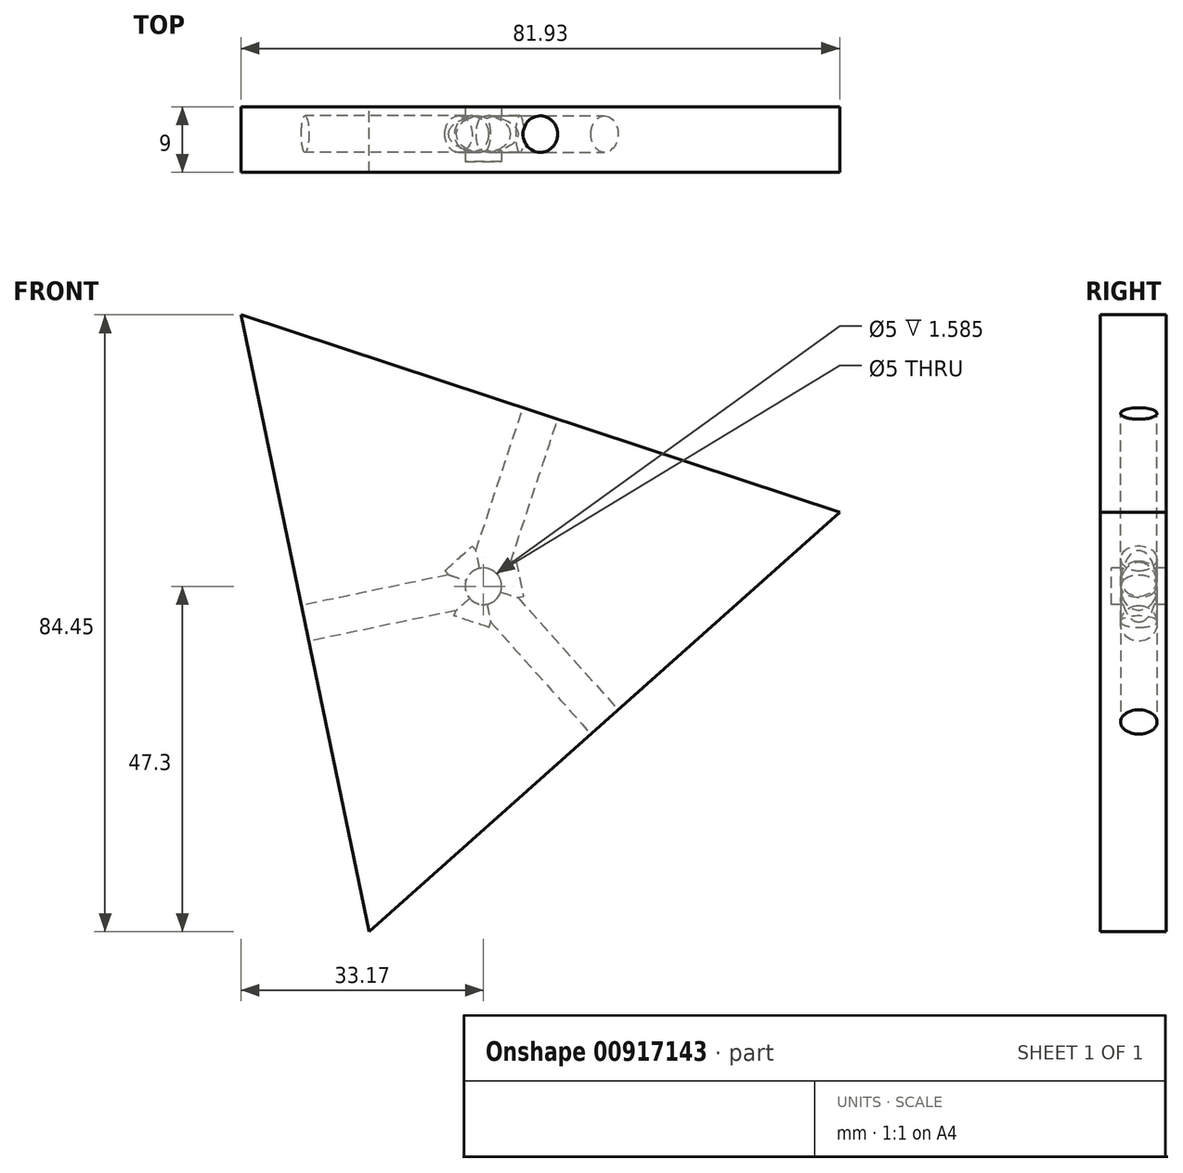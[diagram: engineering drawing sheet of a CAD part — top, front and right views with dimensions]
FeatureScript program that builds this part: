
annotation { "Feature Type Name" : "Feature", "Feature Type Description" : "" }
export const myFeature = defineFeature(function(context is Context, id is Id, definition is map)
    precondition{}
    {
        {
            var Q0;
            Q0=qCreatedBy(makeId("Front.planeOp"),FACE);
            var sketch = newSketch(context, id + "F0", { "sketchPlane" : qUnion([Q0])});
            skCircle(sketch, "E0.cCircle", {"center": v(0, 0) * mm, "radius": 24.9 * mm, "construction": true});
            skLineSegment(sketch, "E0.0", {"start": v(-33.17, 37.15) * mm, "end": v(48.76, 10.15) * mm});
            skLineSegment(sketch, "E0.1", {"start": v(48.76, 10.15) * mm, "end": v(-15.6, -47.3) * mm});
            skLineSegment(sketch, "E0.2", {"start": v(-15.6, -47.3) * mm, "end": v(-33.17, 37.15) * mm});
            skPoint(sketch, "E0.0.midPoint", {"position": v(7.8, 23.65) * mm});
            skSolve(sketch);
        }
        {
            var Q0;
            Q0 = qSketchRegion(id + "F0", true);
            extrude(context, id + "F1", {"entities" : qUnion([Q0]), "depth" : 7.5 * mm, "offsetDistance" : 25 * mm});
        }
        {
            var Q0;
            Q0=makeQuery(id+"F1.opExtrude","CAP_FACE",FACE,{"disambiguationData":[OSD([sQuery(id+"F0.wireOp",EDGE,"E0.0"),sQuery(id+"F0.wireOp",EDGE,"E0.1"),sQuery(id+"F0.wireOp",EDGE,"E0.2")])],"isStart":false});
            var sketch = newSketch(context, id + "F2", { "sketchPlane" : qUnion([Q0])});
            skCircle(sketch, "E1", {"center": v(0, 0) * mm, "radius": 2.5 * mm});
            skSolve(sketch);
        }
        {
            var Q0;
            Q0 = qSketchRegion(id + "F2", true);
            extrude(context, id + "F3", {"entities" : qUnion([Q0]), "operationType" : NewBodyOperationType.REMOVE, "oppositeDirection" : true, "depth" : 25 * mm, "offsetDistance" : 25 * mm});
        }
        {
            var Q0;
            Q0=makeQuery(id+"F1.opExtrude","SWEPT_FACE",FACE,{"disambiguationData":[OSD([sQuery(id+"F0.wireOp",EDGE,"E0.2")])]});
            var sketch = newSketch(context, id + "F4", { "sketchPlane" : qUnion([Q0])});
            skLineSegment(sketch, "E2", {"start": v(7.5, 0) * mm, "end": v(0, 0) * mm, "construction": true});
            skLineSegment(sketch, "E3", {"start": v(3.75, 43.13) * mm, "end": v(3.75, -43.13) * mm, "construction": true});
            skCircle(sketch, "E4", {"center": v(3.75, 0) * mm, "radius": 2.5 * mm});
            skSolve(sketch);
        }
        {
            var Q0;
            Q0 = qSketchRegion(id + "F4", true);
            extrude(context, id + "F5", {"entities" : qUnion([Q0]), "operationType" : NewBodyOperationType.REMOVE, "oppositeDirection" : true, "depth" : 30 * mm, "offsetDistance" : 25 * mm});
        }
        {
            var Q0;
            Q0=makeQuery(id+"F1.opExtrude","SWEPT_FACE",FACE,{"disambiguationData":[OSD([sQuery(id+"F0.wireOp",EDGE,"E0.0")])]});
            var sketch = newSketch(context, id + "F6", { "sketchPlane" : qUnion([Q0])});
            skLineSegment(sketch, "E5", {"start": v(43.13, -3.75) * mm, "end": v(-43.13, -3.75) * mm, "construction": true});
            skLineSegment(sketch, "E6", {"start": v(0, -7.5) * mm, "end": v(0, 0) * mm, "construction": true});
            skCircle(sketch, "E7", {"center": v(0, -3.75) * mm, "radius": 2.5 * mm});
            skSolve(sketch);
        }
        {
            var Q0;
            Q0 = qSketchRegion(id + "F6", true);
            extrude(context, id + "F7", {"entities" : qUnion([Q0]), "operationType" : NewBodyOperationType.REMOVE, "oppositeDirection" : true, "depth" : 30 * mm, "offsetDistance" : 25 * mm});
        }
        {
            var Q0;
            Q0=makeQuery(id+"F1.opExtrude","SWEPT_FACE",FACE,{"disambiguationData":[OSD([sQuery(id+"F0.wireOp",EDGE,"E0.1")])]});
            var sketch = newSketch(context, id + "F8", { "sketchPlane" : qUnion([Q0])});
            skLineSegment(sketch, "E8", {"start": v(43.13, 3.75) * mm, "end": v(-43.13, 3.75) * mm, "construction": true});
            skLineSegment(sketch, "E9", {"start": v(0, 0) * mm, "end": v(0, 7.5) * mm, "construction": true});
            skCircle(sketch, "E10", {"center": v(0, 3.75) * mm, "radius": 2.5 * mm});
            skSolve(sketch);
        }
        {
            var Q0;
            Q0 = qSketchRegion(id + "F8", true);
            extrude(context, id + "F9", {"entities" : qUnion([Q0]), "operationType" : NewBodyOperationType.REMOVE, "oppositeDirection" : true, "depth" : 30 * mm, "offsetDistance" : 25 * mm});
        }
        {
            var Q0;
            Q0=makeQuery(id+"F1.opExtrude","CAP_FACE",FACE,{"disambiguationData":[OSD([sQuery(id+"F0.wireOp",EDGE,"E0.0"),sQuery(id+"F0.wireOp",EDGE,"E0.1"),sQuery(id+"F0.wireOp",EDGE,"E0.2")])],"isStart":false});
            var sketch = newSketch(context, id + "F10", { "sketchPlane" : qUnion([Q0])});
            skCircle(sketch, "E11.cCircle", {"center": v(0, 0) * mm, "radius": 24.9 * mm, "construction": true});
            skLineSegment(sketch, "E11.0", {"start": v(-33.17, 37.15) * mm, "end": v(48.76, 10.15) * mm});
            skLineSegment(sketch, "E11.1", {"start": v(48.76, 10.15) * mm, "end": v(-15.6, -47.3) * mm});
            skLineSegment(sketch, "E11.2", {"start": v(-15.6, -47.3) * mm, "end": v(-33.17, 37.15) * mm});
            skPoint(sketch, "E11.0.midPoint", {"position": v(7.8, 23.65) * mm});
            skSolve(sketch);
        }
        {
            var Q0;
            Q0 = qSketchRegion(id + "F10", true);
            extrude(context, id + "F11", {"entities" : qUnion([Q0]), "operationType" : NewBodyOperationType.ADD, "depth" : 1.5 * mm, "offsetDistance" : 25 * mm});
        }
    });
